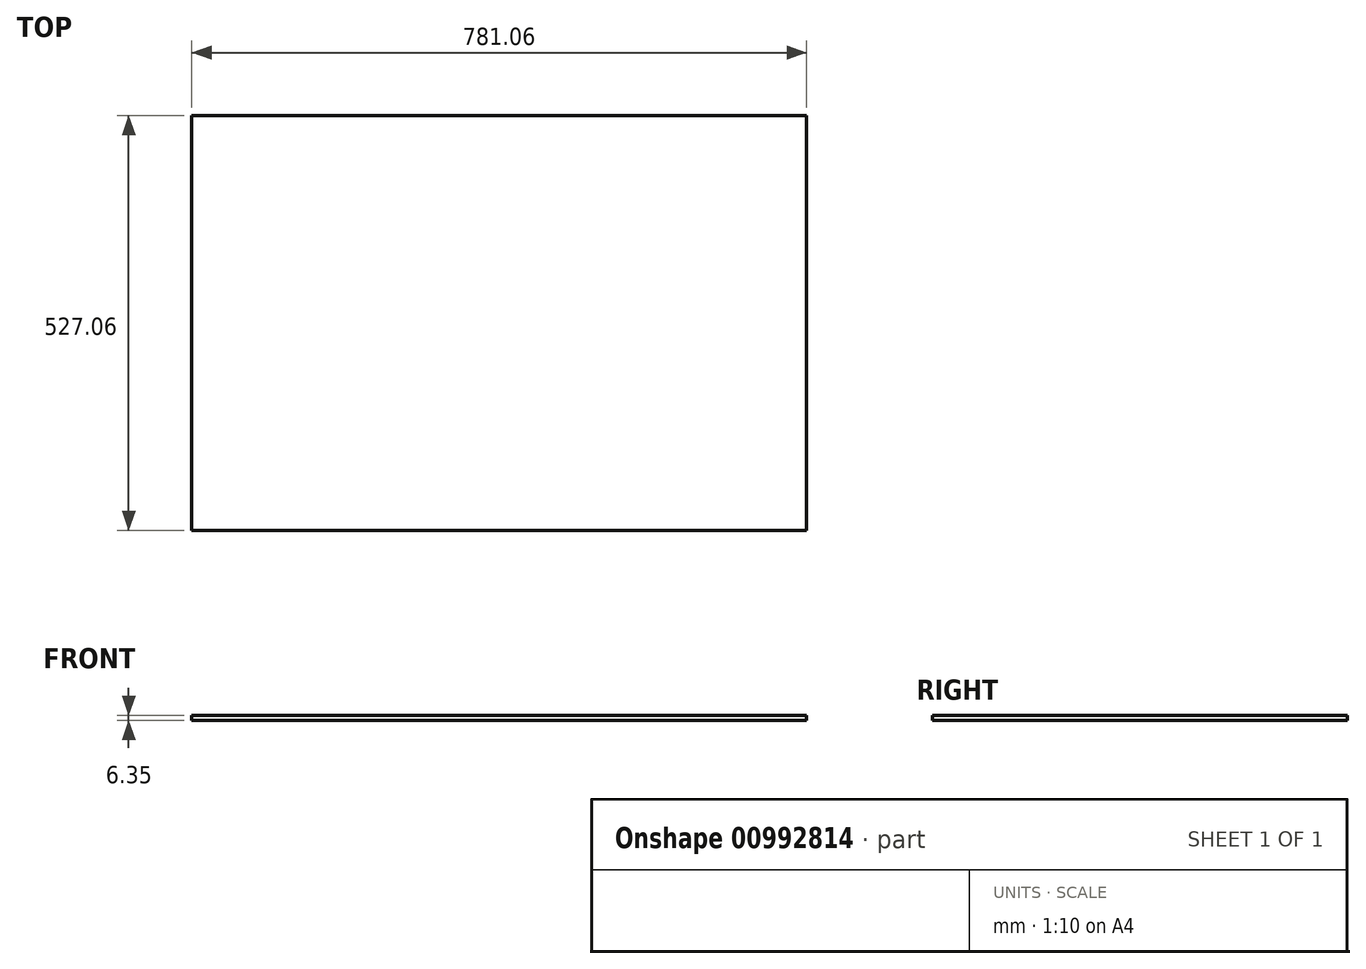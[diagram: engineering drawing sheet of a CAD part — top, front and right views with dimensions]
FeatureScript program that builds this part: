
annotation { "Feature Type Name" : "Feature", "Feature Type Description" : "" }
export const myFeature = defineFeature(function(context is Context, id is Id, definition is map)
    precondition{}
    {
        {
            var Q0;
            Q0=qCreatedBy(makeId("Top.planeOp"),FACE);
            var sketch = newSketch(context, id + "F0", { "sketchPlane" : qUnion([Q0])});
            skLineSegment(sketch, "E0", {"start": v(0, -263.53) * mm, "end": v(0, 263.52) * mm, "construction": true});
            skLineSegment(sketch, "E1", {"start": v(390.53, 0) * mm, "end": v(-390.53, 0) * mm, "construction": true});
            skLineSegment(sketch, "E2.bottom", {"start": v(-390.53, 263.52) * mm, "end": v(390.53, 263.52) * mm});
            skLineSegment(sketch, "E2.top", {"start": v(-390.53, -263.52) * mm, "end": v(390.53, -263.52) * mm});
            skLineSegment(sketch, "E2.left", {"start": v(-390.53, 263.52) * mm, "end": v(-390.53, -263.52) * mm});
            skLineSegment(sketch, "E2.right", {"start": v(390.53, 263.52) * mm, "end": v(390.53, -263.52) * mm});
            skPoint(sketch, "E2.middle", {"position": v(0, 0) * mm});
            skSolve(sketch);
        }
        {
            var Q0;
            Q0 = qSketchRegion(id + "F0", true);
            extrude(context, id + "F1", {"entities" : qUnion([Q0]), "depth" : 6.35 * mm, "offsetDistance" : 25.4 * mm});
        }
    });
